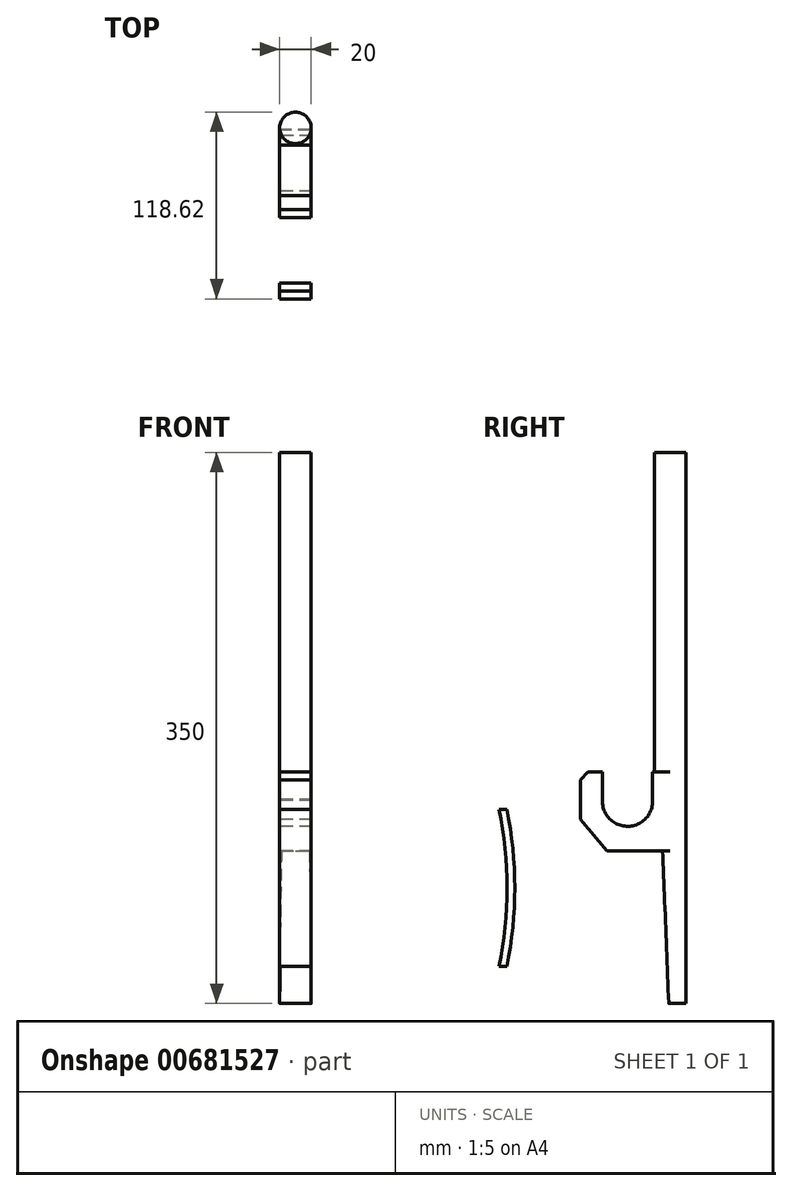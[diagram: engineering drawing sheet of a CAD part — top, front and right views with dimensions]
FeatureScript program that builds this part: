
annotation { "Feature Type Name" : "Feature", "Feature Type Description" : "" }
export const myFeature = defineFeature(function(context is Context, id is Id, definition is map)
    precondition{}
    {
        {
            var Q0;
            Q0=qCreatedBy(makeId("Right.planeOp"),FACE);
            var sketch = newSketch(context, id + "F0", { "sketchPlane" : qUnion([Q0])});
            skLineSegment(sketch, "E0", {"start": v(-0.27, 3.05) * mm, "end": v(39.73, 3.05) * mm});
            skLineSegment(sketch, "E1", {"start": v(39.73, 3.05) * mm, "end": v(39.73, 53.05) * mm});
            skArc(sketch, "E2", {"start": v(-3.27, 34.94) * mm, "mid": v(13.08, 18.55) * mm, "end": v(28.69, 35.65) * mm});
            skLineSegment(sketch, "E3", {"start": v(-3.27, 34.94) * mm, "end": v(-3.27, 53.05) * mm});
            skLineSegment(sketch, "E4", {"start": v(-17.27, 48.05) * mm, "end": v(-12.27, 53.05) * mm});
            skLineSegment(sketch, "E5", {"start": v(-17.27, 48.05) * mm, "end": v(-17.27, 23.05) * mm});
            skLineSegment(sketch, "E6", {"start": v(-12.27, 53.05) * mm, "end": v(-3.27, 53.05) * mm});
            skLineSegment(sketch, "E7", {"start": v(28.69, 53.05) * mm, "end": v(39.73, 53.05) * mm});
            skLineSegment(sketch, "E8", {"start": v(28.69, 53.05) * mm, "end": v(28.69, 35.65) * mm});
            skLineSegment(sketch, "E9", {"start": v(-17.27, 23.05) * mm, "end": v(-0.27, 3.05) * mm});
            skSolve(sketch);
        }
        {
            var Q0;
            Q0=makeQuery(id+"F0.imprint","IMPRINT",FACE,{"disambiguationData":[TD([[makeQuery(id+"F0.imprint","IMPRINT",EDGE,{"derivedFrom":sQuery(id+"F0.wireOp",EDGE,"E0")}),1.0]])]});
            extrude(context, id + "F1", {"entities" : qUnion([Q0]), "depth" : 10 * mm, "offsetDistance" : 25 * mm});
        }
        {
            var Q0;
            Q0=qCreatedBy(makeId("Right.planeOp"),FACE);
            var sketch = newSketch(context, id + "F2", { "sketchPlane" : qUnion([Q0])});
            skLineSegment(sketch, "E10.bottom", {"start": v(39.73, 256.05) * mm, "end": v(29.73, 256.05) * mm});
            skLineSegment(sketch, "E10.top", {"start": v(39.73, -93.95) * mm, "end": v(29.73, -93.95) * mm});
            skLineSegment(sketch, "E10.left", {"start": v(39.73, 256.05) * mm, "end": v(39.73, -93.95) * mm});
            skLineSegment(sketch, "E10.right", {"start": v(29.73, 256.05) * mm, "end": v(29.73, -93.95) * mm});
            skSolve(sketch);
        }
        {
            var Q0;
            Q0 = qSketchRegion(id + "F0", true);
            extrude(context, id + "F3", {"entities" : qUnion([Q0]), "operationType" : NewBodyOperationType.ADD, "depth" : -10 * mm, "offsetDistance" : 25 * mm});
        }
        {
            var Q0;
            Q0=qCreatedBy(makeId("Right.planeOp"),FACE);
            var sketch = newSketch(context, id + "F4", { "sketchPlane" : qUnion([Q0])});
            skPoint(sketch, "E11.orphan", {"position": v(28.92, 3.06) * mm});
            skLineSegment(sketch, "E12", {"start": v(28.92, 3.06) * mm, "end": v(28.92, -93.94) * mm});
            skLineSegment(sketch, "E13", {"start": v(35.04, 3.06) * mm, "end": v(38.92, -93.94) * mm});
            skLineSegment(sketch, "E14", {"start": v(38.92, -93.94) * mm, "end": v(34.92, -94.1) * mm});
            skLineSegment(sketch, "E15", {"start": v(28.92, -93.94) * mm, "end": v(38.92, -93.94) * mm});
            skLineSegment(sketch, "E16", {"start": v(31.04, 3.06) * mm, "end": v(34.92, -94.1) * mm});
            skLineSegment(sketch, "E17", {"start": v(28.92, 3.06) * mm, "end": v(35.04, 3.06) * mm});
            skSolve(sketch);
        }
        {
            var Q0;
            Q0=makeQuery(id+"F2.imprint","IMPRINT",FACE,{"disambiguationData":[TD([[makeQuery(id+"F2.imprint","IMPRINT",EDGE,{"derivedFrom":sQuery(id+"F2.wireOp",EDGE,"E10.bottom")}),1.0]])]});
            var Q1;
            Q1=sQuery(id+"F2.wireOp",EDGE,"E10.left");
            revolve(context, id + "F5", {"operationType" : NewBodyOperationType.ADD, "entities" : qUnion([Q0]), "axis" : qUnion([Q1]), "revolveType" : RevolveType.FULL});
        }
        {
            var Q0;
            Q0 = qSketchRegion(id + "F4", true);
            extrude(context, id + "F6", {"entities" : qUnion([Q0]), "operationType" : NewBodyOperationType.REMOVE, "oppositeDirection" : true, "depth" : 30 * mm, "offsetDistance" : 25 * mm});
        }
        {
            var Q0;
            Q0 = qSketchRegion(id + "F4", true);
            extrude(context, id + "F7", {"entities" : qUnion([Q0]), "operationType" : NewBodyOperationType.REMOVE, "oppositeDirection" : true, "depth" : -30 * mm, "offsetDistance" : 25 * mm});
        }
        {
            var Q0;
            Q0=qCreatedBy(makeId("Right.planeOp"),FACE);
            var sketch = newSketch(context, id + "F8", { "sketchPlane" : qUnion([Q0])});
            skLineSegment(sketch, "E18", {"start": v(-68.89, -70.57) * mm, "end": v(-63.89, -70.57) * mm});
            skLineSegment(sketch, "E19", {"start": v(-63.89, 29.43) * mm, "end": v(-68.89, 29.43) * mm});
            skArc(sketch, "E20", {"start": v(-68.89, -70.57) * mm, "mid": v(-63.85, -20.57) * mm, "end": v(-68.89, 29.43) * mm});
            skArc(sketch, "E21", {"start": v(-63.89, -70.57) * mm, "mid": v(-58.87, -20.57) * mm, "end": v(-63.89, 29.43) * mm});
            skSolve(sketch);
        }
        {
            var Q0;
            Q0 = qSketchRegion(id + "F8", true);
            extrude(context, id + "F9", {"entities" : qUnion([Q0]), "depth" : 10 * mm, "offsetDistance" : 25 * mm});
        }
        {
            var Q0;
            Q0 = qSketchRegion(id + "F8", true);
            extrude(context, id + "F10", {"entities" : qUnion([Q0]), "operationType" : NewBodyOperationType.ADD, "depth" : -10 * mm, "offsetDistance" : 25 * mm});
        }
        {
            var Q0;
            Q0 = qSketchRegion(id + "F0", true);
            extrude(context, id + "F11", {"entities" : qUnion([Q0]), "operationType" : NewBodyOperationType.ADD, "depth" : 10 * mm, "offsetDistance" : 25 * mm});
        }
    });
